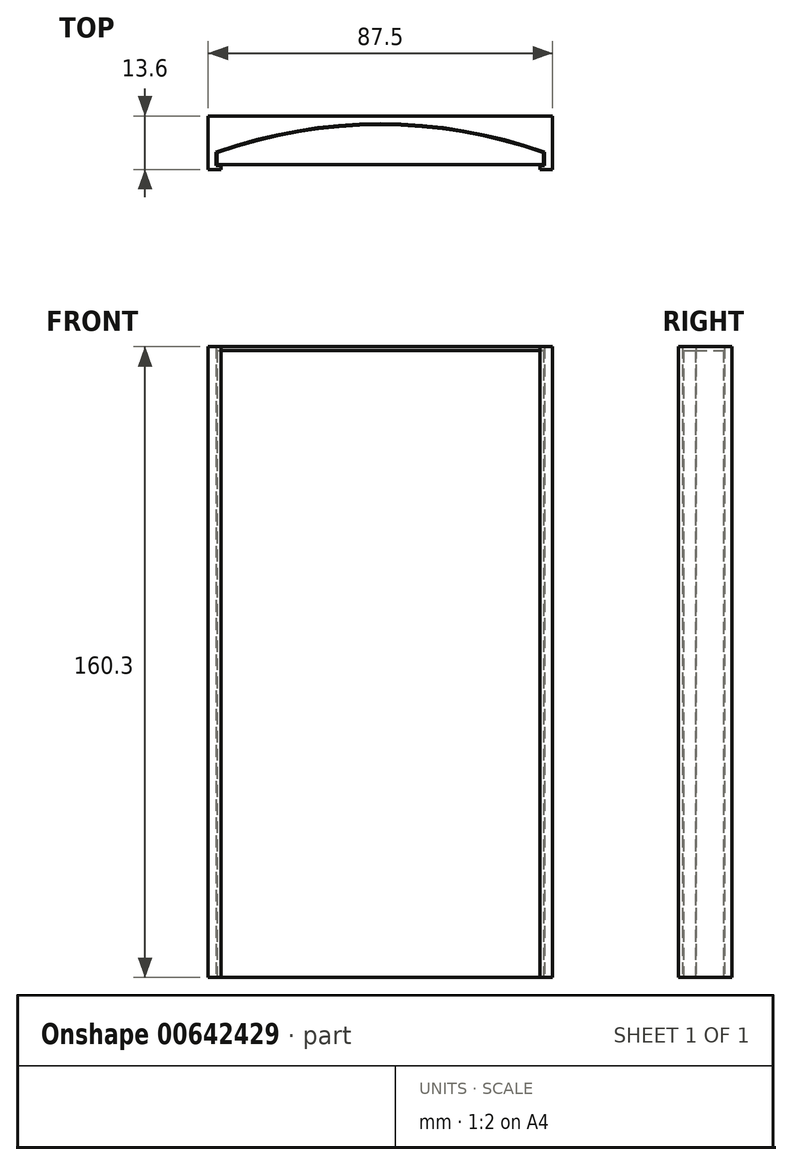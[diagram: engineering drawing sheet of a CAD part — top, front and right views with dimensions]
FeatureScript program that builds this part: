
annotation { "Feature Type Name" : "Feature", "Feature Type Description" : "" }
export const myFeature = defineFeature(function(context is Context, id is Id, definition is map)
    precondition{}
    {
        {
            var Q0;
            Q0=qCreatedBy(makeId("Top.planeOp"),FACE);
            var sketch = newSketch(context, id + "F0", { "sketchPlane" : qUnion([Q0])});
            skLineSegment(sketch, "E0", {"start": v(0, 0) * mm, "end": v(41.5, 0) * mm});
            skLineSegment(sketch, "E1", {"start": v(0, 0) * mm, "end": v(0, 3) * mm});
            skArc(sketch, "E2", {"start": v(41.5, 10.1) * mm, "mid": v(20.45, 8.31) * mm, "end": v(0, 3) * mm});
            skLineSegment(sketch, "E3", {"start": v(41.5, 0) * mm, "end": v(41.5, 10.1) * mm, "construction": true});
            skLineSegment(sketch, "E4.MirrorCS", {"start": v(83, 0) * mm, "end": v(83, 3) * mm});
            skArc(sketch, "E5.MirrorCS", {"start": v(41.5, 10.1) * mm, "mid": v(62.55, 8.31) * mm, "end": v(83, 3) * mm});
            skLineSegment(sketch, "E6.MirrorCS", {"start": v(83, 0) * mm, "end": v(41.5, 0) * mm});
            skArc(sketch, "E7.0", {"start": v(41.5, 10.35) * mm, "mid": v(20.32, 8.54) * mm, "end": v(-0.25, 3.18) * mm});
            skLineSegment(sketch, "E7.1", {"start": v(-0.25, 0) * mm, "end": v(-0.25, 3.18) * mm});
            skLineSegment(sketch, "E8", {"start": v(-0.25, 0) * mm, "end": v(-0.25, -0.25) * mm});
            skLineSegment(sketch, "E9", {"start": v(-0.25, -0.25) * mm, "end": v(1, -0.25) * mm});
            skLineSegment(sketch, "E10", {"start": v(1, -0.25) * mm, "end": v(1, -1.25) * mm});
            skLineSegment(sketch, "E11", {"start": v(1, -1.25) * mm, "end": v(-2.25, -1.25) * mm});
            skLineSegment(sketch, "E12", {"start": v(-2.25, -1.25) * mm, "end": v(-2.25, -1.25) * mm});
            skLineSegment(sketch, "E13", {"start": v(-2.25, 12.35) * mm, "end": v(-2.25, -1.25) * mm});
            skLineSegment(sketch, "E14", {"start": v(-2.25, 12.35) * mm, "end": v(41.5, 12.35) * mm});
            skLineSegment(sketch, "E15.MirrorCS", {"start": v(85.25, 12.35) * mm, "end": v(41.5, 12.35) * mm});
            skArc(sketch, "E16.MirrorCS", {"start": v(41.5, 10.35) * mm, "mid": v(62.68, 8.54) * mm, "end": v(83.25, 3.18) * mm});
            skLineSegment(sketch, "E17.MirrorCS", {"start": v(85.25, 12.35) * mm, "end": v(85.25, -1.25) * mm});
            skLineSegment(sketch, "E18.MirrorCS", {"start": v(83.25, 0) * mm, "end": v(83.25, 3.18) * mm});
            skLineSegment(sketch, "E19.MirrorCS", {"start": v(82, -1.25) * mm, "end": v(85.25, -1.25) * mm});
            skLineSegment(sketch, "E20.MirrorCS", {"start": v(83.25, -0.25) * mm, "end": v(82, -0.25) * mm});
            skLineSegment(sketch, "E21.MirrorCS", {"start": v(82, -0.25) * mm, "end": v(82, -1.25) * mm});
            skLineSegment(sketch, "E22.MirrorCS", {"start": v(83.25, 0) * mm, "end": v(83.25, -0.25) * mm});
            skSolve(sketch);
        }
        {
            var Q0;
            Q0=makeQuery(id+"F0.imprint","IMPRINT",FACE,{"disambiguationData":[TD([[makeQuery(id+"F0.imprint","IMPRINT",EDGE,{"derivedFrom":sQuery(id+"F0.wireOp",EDGE,"E0")}),1.0]])]});
            extrude(context, id + "F1", {"entities" : qUnion([Q0]), "depth" : 159.3 * mm, "offsetDistance" : 25 * mm});
        }
        {
            var Q0;
            Q0=makeQuery(id+"F1.opExtrude","CAP_FACE",FACE,{"disambiguationData":[OSD([sQuery(id+"F0.wireOp",EDGE,"E0"),sQuery(id+"F0.wireOp",EDGE,"E1"),sQuery(id+"F0.wireOp",EDGE,"E2"),sQuery(id+"F0.wireOp",EDGE,"E4.MirrorCS"),sQuery(id+"F0.wireOp",EDGE,"E5.MirrorCS"),sQuery(id+"F0.wireOp",EDGE,"E6.MirrorCS")])],"isStart":false});
            cPlane(context, id + "F2", {"entities" : qUnion([Q0]), "cplaneType" : CPlaneType.OFFSET, "offset" : 1 * mm, "width" : 150 * mm, "height" : 150 * mm});
        }
        {
            var Q0;
            Q0=makeQuery(id+"F0.imprint","IMPRINT",FACE,{"disambiguationData":[TD([[makeQuery(id+"F0.imprint","IMPRINT",EDGE,{"derivedFrom":sQuery(id+"F0.wireOp",EDGE,"E7.0")}),-1.0]])]});
            var Q1;
            Q1=qCreatedBy(id+"F2.planeOp",FACE);
            extrude(context, id + "F3", {"entities" : qUnion([Q0]), "endBound" : BoundingType.UP_TO_SURFACE, "depth" : 25 * mm, "endBoundEntityFace" : qUnion([Q1]), "offsetDistance" : 25 * mm});
        }
    });
